# Revit family: okamura_MS9ZGM_ライズフィット3_楕円形 ブラック支柱 ポリッシュ脚
name_source: partatom
category: Furniture
revit_build: Autodesk Revit 2016 (Build: 20150714_1515(x64)
units: mm (PartAtom-declared; Revit-internal decimal feet)

## family parameters
Always vertical = Yes
Cut with Voids When Loaded = No
OmniClass Number = 23.40.20.00
OmniClass Title = General Furniture and Specialties
Room Calculation Point = No
Shared = No
Work Plane-Based = No

## types (7) — shared parameters
Assembly Code = E2020200
Base = okm_FX4
Casters = okm_G155
Column = okm_Z25
D = 626 mm  [stored 2.05381 ft]
H = 690 mm  [stored 2.26378 ft]
Keynote = 12490
Kind = Side Table
Manufacturer = Okamura Corporation
Product Categories = Work Tool
URL = http://www.okamura.co.jp
W = 735 mm

## per-type parameters (varying)
| type | Arm | Product Code/Color | Tabletop |
| MG99(White) | okm_ZA75 | MS9ZGM_MG99 | okm_MG07 |
| MK37(Neowood Light) | okm_Z975 | MS9ZGM_MK37 | okm_MK17 |
| MK38(Neowood Medium) | okm_Z975 | MS9ZGM_MK38 | okm_MK18 |
| MK39(Neowood Dark) | okm_Z975 | MS9ZGM_MK39 | okm_MK19 |
| MX61(Prizewood Light) | okm_Z975 | MS9ZGM_MX61 | okm_MX51 |
| MX62(Prizewood Medium) | okm_Z975 | MS9ZGM_MX62 | okm_MX52 |
| MX63(Prizewood Dark) | okm_Z975 | MS9ZGM_MX63 | okm_MX53 |

note: [stored X ft] marks values corroborated as IEEE doubles in the binary element streams (Revit-internal decimal feet)
